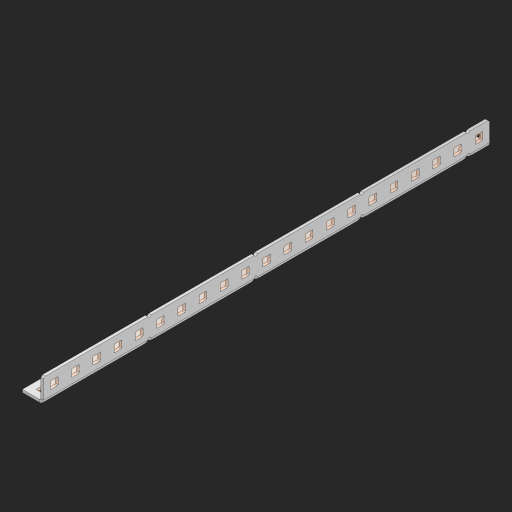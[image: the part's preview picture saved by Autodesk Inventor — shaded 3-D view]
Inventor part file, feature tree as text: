
AUTODESK INVENTOR PART (.ipt)
format: ipt  version: 2023 (Build 270158000, 158)  size: 795,136 bytes
history: native  units: in
note: dims shown in document units (in); Inventor stores cm internally (conversion verified against a paired STEP export)
features: other x47, extrude x41, sheet_metal_op x10, sketch x8, mirror x1, pattern_linear x1, chamfer x1
ambient origin geometry x8: Origin, YZ Plane, XZ Plane, XY Plane, X Axis, Y Axis, Z Axis, Center Point
bodies: Solid1 (feature_tree), Body (feature_tree)
feature tree (109):
  other  "Flange Pattern Plane"
  sheet_metal_op  "Flange Pattern"
  sheet_metal_op  "Body Pattern"
  other  "Arc Length"
  mirror  "Notch Mirror"
  pattern_linear  "Notch Pattern"  Spacing1=0.25in  [1 undecoded]
  chamfer  "End Chamfer"
  extrude  "Half Cut"  Depth=0.0625in
  sketch  "Sketch1"  dims[d0=1.5in]
  other  "Plate1"
  sketch  "Sketch2"  dims[d1=10.5in]
  other  "Plate2"
  sheet_metal_op  "Bend1"
  sheet_metal_op  "Corner1"
  sketch  "Sketch3"  dims[d2=0.0625in]
  other  "Flange Pattern Sketch"
  sketch  "Sketch7"  dims[d3=0.0625in]
  other  "Srf1"
  other  "Srf2"
  sketch  "Sketch8"  dims[d4=0.0312in]
  sketch  "Sketch9"  dims[d5=0.125in]
  other  "Srf91"
  sheet_metal_op  "Body Pattern Sketch"
  other  "Srf92"
  sketch  "Sketch13"  dims[d6=0.0625in]
  sketch  "Sketch14"  dims[d7=0.5in d8=90.0deg d9=0.0312in d10=0.25in d11=0.0625in d12=0.0625in d16=0.182in d17=0.02in d18=0.0625in d19=0.0in d20=0.25in d21=0.25in d46=0.172in d47=1.0in d48=0.0in d49=0.182in d50=0.02in d51=0.25in d52=0.25in d53=0.0625in d54=0.0in d55=0.172in d56=1.0in d57=0.0in d60=8.2677in d62=0.5in d63=0.3937in d65=0.5in d85=0.1473in d86=0.1782in d88=0.04in d89=0.0625in d90=0.0in d91=0.04in d92=0.0491in d95=2.5in d96=0.04in d97=0.25in d98=45.0deg d101=0.0in d102=2.497in d131=0.5in d132=8.2677in d134=0.5in d139=0.5in]
  other  "Srf856"
  other  "Srf1310"
  other  "Srf1311"
  other  "Srf1312"
  other  "Srf1376"
  other  "Srf1377"
  other  "Srf1728"
  other  "Srf1755"
  other  "Srf1878"
  other  "Srf1879"
  other  "Srf1880"
  other  "Srf1881"
  other  "Srf1882"
  other  "Srf1883"
  other  "Srf1884"
  other  "Srf1885"
  other  "Srf1886"
  other  "Srf1887"
  other  "Srf1888"
  other  "Srf1889"
  other  "Srf1890"
  other  "Srf1891"
  other  "Srf1892"
  other  "Srf1942"
  other  "Srf1943"
  other  "Srf1944"
  other  "Srf1945"
  other  "Srf1946"
  other  "Srf1947"
  other  "Srf1948"
  other  "Srf1949"
  other  "Srf1950"
  other  "Srf1951"
  other  "Srf1952"
  other  "Srf1953"
  other  "Srf1954"
  other  "Srf1955"
  other  "Srf1956"
  sheet_metal_op  "Flange Stamp"
  sheet_metal_op  "Flange Circle"
  sheet_metal_op  "Body Stamp"
  sheet_metal_op  "Body Circle"
  sheet_metal_op  "Notch"
  extrude  "ExtrusionSrf2"  Depth=0.0625in
  extrude  "ExtrusionSrf92"  Depth=0.5in
  extrude  "ExtrusionSrf856"  Depth=0.02in
  extrude  "ExtrusionSrf1310"  Depth=0.0625in
  extrude  "ExtrusionSrf1311"  TaperAngle=0.0deg  [1 undecoded]
  extrude  "ExtrusionSrf1312"  Depth=0.5in
  extrude  "ExtrusionSrf1376"  Depth=0.5in
  extrude  "ExtrusionSrf1377"  Depth=0.5in
  extrude  "ExtrusionSrf1728"  Depth=0.5in TaperAngle=0.0deg
  extrude  "ExtrusionSrf1755"  Depth=0.5in
  extrude  "ExtrusionSrf1878"  Depth=0.02in
  extrude  "ExtrusionSrf1879"  Depth=0.5in
  extrude  "ExtrusionSrf1880"  Depth=0.5in
  extrude  "ExtrusionSrf1881"  Depth=0.0625in
  extrude  "ExtrusionSrf1882"  TaperAngle=0.0deg  [1 undecoded]
  extrude  "ExtrusionSrf1883"  Depth=0.5in
  extrude  "ExtrusionSrf1884"  Depth=0.5in TaperAngle=0.0deg
  extrude  "ExtrusionSrf1885"  Depth=0.5in
  extrude  "ExtrusionSrf1886"  Depth=0.5in
  extrude  "ExtrusionSrf1887"  Depth=0.5in
  extrude  "ExtrusionSrf1888"  Depth=0.5in
  extrude  "ExtrusionSrf1889"  Depth=0.5in
  extrude  "ExtrusionSrf1890"  Depth=0.0625in
  extrude  "ExtrusionSrf1891"  TaperAngle=0.0deg  [1 undecoded]
  extrude  "ExtrusionSrf1892"  Depth=0.5in
  extrude  "ExtrusionSrf1942"  Depth=0.5in
  extrude  "ExtrusionSrf1943"  Depth=0.5in
  extrude  "ExtrusionSrf1944"  Depth=0.5in TaperAngle=45.0deg
  extrude  "ExtrusionSrf1945"  TaperAngle=0.0deg  [1 undecoded]
  extrude  "ExtrusionSrf1946"  Depth=0.5in
  extrude  "ExtrusionSrf1947"  Depth=0.5in
  extrude  "ExtrusionSrf1948"  Depth=0.5in
  extrude  "ExtrusionSrf1949"  Depth=0.5in
  extrude  "ExtrusionSrf1950"  Depth=0.5in
  extrude  "ExtrusionSrf1951"  [1 undecoded]
  extrude  "ExtrusionSrf1952"  [1 undecoded]
  extrude  "ExtrusionSrf1953"  [1 undecoded]
  extrude  "ExtrusionSrf1954"  [1 undecoded]
  extrude  "ExtrusionSrf1955"  [1 undecoded]
  extrude  "ExtrusionSrf1956"  [1 undecoded]
note: 11 required parameter values undecoded (feature->parameter linkage not recoverable at this tier; creation-order binding heuristic only, values carry confidence <= 0.55)
